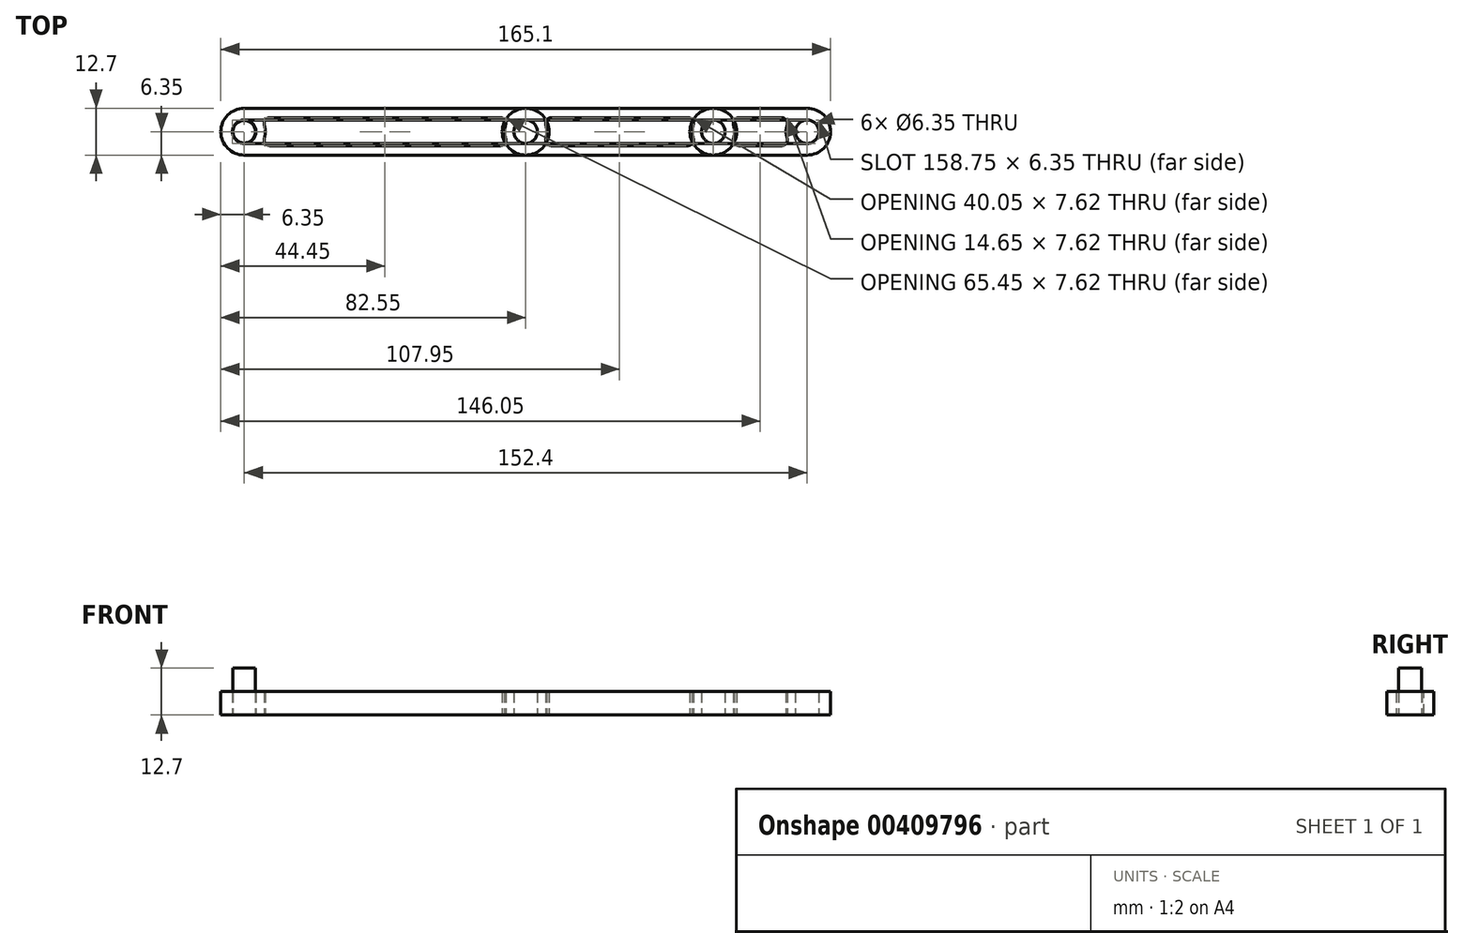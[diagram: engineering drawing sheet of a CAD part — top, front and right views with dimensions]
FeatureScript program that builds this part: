
annotation { "Feature Type Name" : "Feature", "Feature Type Description" : "" }
export const myFeature = defineFeature(function(context is Context, id is Id, definition is map)
    precondition{}
    {
        {
            var Q0;
            Q0=qCreatedBy(makeId("Top.planeOp"),FACE);
            var sketch = newSketch(context, id + "F0", { "sketchPlane" : qUnion([Q0])});
            skCircle(sketch, "E0", {"center": v(0, 0) * mm, "radius": 3.18 * mm});
            skCircle(sketch, "E1", {"center": v(0, 0) * mm, "radius": 6.35 * mm});
            skCircle(sketch, "E2", {"center": v(76.2, 0) * mm, "radius": 3.18 * mm});
            skCircle(sketch, "E3", {"center": v(127, 0) * mm, "radius": 3.18 * mm});
            skCircle(sketch, "E4", {"center": v(152.4, 0) * mm, "radius": 3.18 * mm});
            skCircle(sketch, "E5", {"center": v(76.2, 0) * mm, "radius": 6.35 * mm});
            skCircle(sketch, "E6", {"center": v(127, 0) * mm, "radius": 6.35 * mm});
            skCircle(sketch, "E7", {"center": v(152.4, 0) * mm, "radius": 6.35 * mm});
            skLineSegment(sketch, "E8", {"start": v(0, 6.35) * mm, "end": v(152.4, 6.35) * mm});
            skLineSegment(sketch, "E9", {"start": v(0, -6.35) * mm, "end": v(152.4, -6.35) * mm});
            skCircle(sketch, "E10", {"center": v(0, 0) * mm, "radius": 3.05 * mm});
            skLineSegment(sketch, "E11", {"start": v(0, 3.18) * mm, "end": v(152.4, 3.17) * mm});
            skLineSegment(sketch, "E12", {"start": v(0, -3.17) * mm, "end": v(152.4, -3.18) * mm});
            skSolve(sketch);
        }
        {
            var Q0;
            {var subQ0=sQuery(id+"F0.wireOp",EDGE,"E8");var subQ1=sQuery(id+"F0.wireOp",EDGE,"E1");var subQ2=makeQuery(id+"F0.imprint","INTERSECT",VERTEX,{"derivedFrom":[subQ1,subQ0]});Q0=makeQuery(id+"F0.imprint","IMPRINT",FACE,{"disambiguationData":[TD([[makeQuery(id+"F0.imprint","IMPRINT",EDGE,{"disambiguationData":[TD([[subQ2,1.0]])],"derivedFrom":subQ1}),-1.0]])]});}
            var Q1;
            Q1=makeQuery(id+"F0.imprint","IMPRINT",FACE,{"disambiguationData":[TD([[makeQuery(id+"F0.imprint","IMPRINT",EDGE,{"derivedFrom":sQuery(id+"F0.wireOp",EDGE,"E2")}),-1.0]])]});
            var Q2;
            Q2=makeQuery(id+"F0.imprint","IMPRINT",FACE,{"disambiguationData":[TD([[makeQuery(id+"F0.imprint","IMPRINT",EDGE,{"derivedFrom":sQuery(id+"F0.wireOp",EDGE,"E0")}),-1.0]])]});
            var Q3;
            {var subQ5=sQuery(id+"F0.wireOp",EDGE,"E11");var subQ7=sQuery(id+"F0.wireOp",EDGE,"E0");var subQ8=makeQuery(id+"F0.imprint","INTERSECT",VERTEX,{"derivedFrom":[subQ7,subQ5]});Q3=makeQuery(id+"F0.imprint","IMPRINT",FACE,{"disambiguationData":[TD([[makeQuery(id+"F0.imprint","IMPRINT",EDGE,{"disambiguationData":[TD([[subQ8,-1.0]])],"derivedFrom":subQ7}),-1.0]])]});}
            var Q4;
            {var subQ0=sQuery(id+"F0.wireOp",EDGE,"E11");var subQ1=sQuery(id+"F0.wireOp",EDGE,"E1");var subQ2=makeQuery(id+"F0.imprint","INTERSECT",VERTEX,{"derivedFrom":[subQ1,subQ0]});Q4=makeQuery(id+"F0.imprint","IMPRINT",FACE,{"disambiguationData":[TD([[makeQuery(id+"F0.imprint","IMPRINT",EDGE,{"disambiguationData":[TD([[subQ2,1.0]])],"derivedFrom":subQ1}),-1.0]])]});}
            var Q5;
            {var subQ0=sQuery(id+"F0.wireOp",EDGE,"E9");var subQ1=sQuery(id+"F0.wireOp",EDGE,"E1");var subQ2=makeQuery(id+"F0.imprint","INTERSECT",VERTEX,{"derivedFrom":[subQ1,subQ0]});Q5=makeQuery(id+"F0.imprint","IMPRINT",FACE,{"disambiguationData":[TD([[makeQuery(id+"F0.imprint","IMPRINT",EDGE,{"disambiguationData":[TD([[subQ2,-1.0]])],"derivedFrom":subQ1}),-1.0]])]});}
            var Q6;
            {var subQ0=sQuery(id+"F0.wireOp",EDGE,"E5");var subQ1=makeQuery(id+"F0.imprint","INTERSECT",VERTEX,{"derivedFrom":[subQ0,sQuery(id+"F0.wireOp",EDGE,"E8")]});Q6=makeQuery(id+"F0.imprint","IMPRINT",FACE,{"disambiguationData":[TD([[makeQuery(id+"F0.imprint","IMPRINT",EDGE,{"disambiguationData":[TD([[subQ1,1.0]])],"derivedFrom":subQ0}),1.0]])]});}
            var Q7;
            {var subQ0=sQuery(id+"F0.wireOp",EDGE,"E5");var subQ1=makeQuery(id+"F0.imprint","INTERSECT",VERTEX,{"derivedFrom":[subQ0,sQuery(id+"F0.wireOp",EDGE,"E9")]});Q7=makeQuery(id+"F0.imprint","IMPRINT",FACE,{"disambiguationData":[TD([[makeQuery(id+"F0.imprint","IMPRINT",EDGE,{"disambiguationData":[TD([[subQ1,1.0]])],"derivedFrom":subQ0}),1.0]])]});}
            extrude(context, id + "F1", {"entities" : qUnion([Q0, Q1, Q2, Q3, Q4, Q5, Q6, Q7]), "depth" : 6.35 * mm});
        }
        {
            var Q0;
            {var subQ0=sQuery(id+"F0.wireOp",EDGE,"E8");var subQ1=sQuery(id+"F0.wireOp",EDGE,"E5");var subQ2=makeQuery(id+"F0.imprint","INTERSECT",VERTEX,{"derivedFrom":[subQ1,subQ0]});Q0=makeQuery(id+"F0.imprint","IMPRINT",FACE,{"disambiguationData":[TD([[makeQuery(id+"F0.imprint","IMPRINT",EDGE,{"disambiguationData":[TD([[subQ2,1.0]])],"derivedFrom":subQ1}),-1.0]])]});}
            var Q1;
            {var subQ0=sQuery(id+"F0.wireOp",EDGE,"E11");var subQ1=sQuery(id+"F0.wireOp",EDGE,"E5");var subQ2=makeQuery(id+"F0.imprint","INTERSECT",VERTEX,{"disambiguationData":[OD(0.0)],"derivedFrom":[subQ1,subQ0]});Q1=makeQuery(id+"F0.imprint","IMPRINT",FACE,{"disambiguationData":[TD([[makeQuery(id+"F0.imprint","IMPRINT",EDGE,{"disambiguationData":[TD([[subQ2,1.0]])],"derivedFrom":subQ1}),-1.0]])]});}
            var Q2;
            {var subQ0=sQuery(id+"F0.wireOp",EDGE,"E9");var subQ1=sQuery(id+"F0.wireOp",EDGE,"E5");var subQ2=makeQuery(id+"F0.imprint","INTERSECT",VERTEX,{"derivedFrom":[subQ1,subQ0]});Q2=makeQuery(id+"F0.imprint","IMPRINT",FACE,{"disambiguationData":[TD([[makeQuery(id+"F0.imprint","IMPRINT",EDGE,{"disambiguationData":[TD([[subQ2,-1.0]])],"derivedFrom":subQ1}),-1.0]])]});}
            var Q3;
            {var subQ0=sQuery(id+"F0.wireOp",EDGE,"E11");var subQ1=sQuery(id+"F0.wireOp",EDGE,"E3");var subQ2=makeQuery(id+"F0.imprint","INTERSECT",VERTEX,{"derivedFrom":[subQ1,subQ0]});Q3=makeQuery(id+"F0.imprint","IMPRINT",FACE,{"disambiguationData":[TD([[makeQuery(id+"F0.imprint","IMPRINT",EDGE,{"disambiguationData":[TD([[subQ2,-1.0]])],"derivedFrom":subQ1}),-1.0]])]});}
            var Q4;
            {var subQ0=sQuery(id+"F0.wireOp",EDGE,"E6");var subQ1=makeQuery(id+"F0.imprint","INTERSECT",VERTEX,{"derivedFrom":[subQ0,sQuery(id+"F0.wireOp",EDGE,"E8")]});Q4=makeQuery(id+"F0.imprint","IMPRINT",FACE,{"disambiguationData":[TD([[makeQuery(id+"F0.imprint","IMPRINT",EDGE,{"disambiguationData":[TD([[subQ1,1.0]])],"derivedFrom":subQ0}),1.0]])]});}
            var Q5;
            {var subQ0=sQuery(id+"F0.wireOp",EDGE,"E11");var subQ1=sQuery(id+"F0.wireOp",EDGE,"E3");var subQ2=makeQuery(id+"F0.imprint","INTERSECT",VERTEX,{"derivedFrom":[subQ1,subQ0]});Q5=makeQuery(id+"F0.imprint","IMPRINT",FACE,{"disambiguationData":[TD([[makeQuery(id+"F0.imprint","IMPRINT",EDGE,{"disambiguationData":[TD([[subQ2,1.0]])],"derivedFrom":subQ1}),-1.0]])]});}
            var Q6;
            {var subQ0=sQuery(id+"F0.wireOp",EDGE,"E6");var subQ1=makeQuery(id+"F0.imprint","INTERSECT",VERTEX,{"derivedFrom":[subQ0,sQuery(id+"F0.wireOp",EDGE,"E9")]});Q6=makeQuery(id+"F0.imprint","IMPRINT",FACE,{"disambiguationData":[TD([[makeQuery(id+"F0.imprint","IMPRINT",EDGE,{"disambiguationData":[TD([[subQ1,1.0]])],"derivedFrom":subQ0}),1.0]])]});}
            var Q7;
            {var subQ0=sQuery(id+"F0.wireOp",EDGE,"E5");var subQ1=makeQuery(id+"F0.imprint","INTERSECT",VERTEX,{"derivedFrom":[subQ0,sQuery(id+"F0.wireOp",EDGE,"E8")]});Q7=makeQuery(id+"F0.imprint","IMPRINT",FACE,{"disambiguationData":[TD([[makeQuery(id+"F0.imprint","IMPRINT",EDGE,{"disambiguationData":[TD([[subQ1,1.0]])],"derivedFrom":subQ0}),1.0]])]});}
            var Q8;
            {var subQ0=sQuery(id+"F0.wireOp",EDGE,"E11");var subQ1=sQuery(id+"F0.wireOp",EDGE,"E2");var subQ2=makeQuery(id+"F0.imprint","INTERSECT",VERTEX,{"derivedFrom":[subQ1,subQ0]});Q8=makeQuery(id+"F0.imprint","IMPRINT",FACE,{"disambiguationData":[TD([[makeQuery(id+"F0.imprint","IMPRINT",EDGE,{"disambiguationData":[TD([[subQ2,-1.0]])],"derivedFrom":subQ1}),-1.0]])]});}
            var Q9;
            {var subQ0=sQuery(id+"F0.wireOp",EDGE,"E11");var subQ1=sQuery(id+"F0.wireOp",EDGE,"E2");var subQ2=makeQuery(id+"F0.imprint","INTERSECT",VERTEX,{"derivedFrom":[subQ1,subQ0]});Q9=makeQuery(id+"F0.imprint","IMPRINT",FACE,{"disambiguationData":[TD([[makeQuery(id+"F0.imprint","IMPRINT",EDGE,{"disambiguationData":[TD([[subQ2,1.0]])],"derivedFrom":subQ1}),-1.0]])]});}
            var Q10;
            {var subQ0=sQuery(id+"F0.wireOp",EDGE,"E5");var subQ1=makeQuery(id+"F0.imprint","INTERSECT",VERTEX,{"derivedFrom":[subQ0,sQuery(id+"F0.wireOp",EDGE,"E9")]});Q10=makeQuery(id+"F0.imprint","IMPRINT",FACE,{"disambiguationData":[TD([[makeQuery(id+"F0.imprint","IMPRINT",EDGE,{"disambiguationData":[TD([[subQ1,1.0]])],"derivedFrom":subQ0}),1.0]])]});}
            extrude(context, id + "F2", {"entities" : qUnion([Q0, Q1, Q2, Q3, Q4, Q5, Q6, Q7, Q8, Q9, Q10]), "depth" : 6.35 * mm});
        }
        {
            var Q0;
            {var subQ0=sQuery(id+"F0.wireOp",EDGE,"E8");var subQ1=sQuery(id+"F0.wireOp",EDGE,"E6");var subQ2=makeQuery(id+"F0.imprint","INTERSECT",VERTEX,{"derivedFrom":[subQ1,subQ0]});Q0=makeQuery(id+"F0.imprint","IMPRINT",FACE,{"disambiguationData":[TD([[makeQuery(id+"F0.imprint","IMPRINT",EDGE,{"disambiguationData":[TD([[subQ2,1.0]])],"derivedFrom":subQ1}),-1.0]])]});}
            var Q1;
            Q1=makeQuery(id+"F0.imprint","IMPRINT",FACE,{"disambiguationData":[TD([[makeQuery(id+"F0.imprint","IMPRINT",EDGE,{"derivedFrom":sQuery(id+"F0.wireOp",EDGE,"E3")}),-1.0]])]});
            var Q2;
            Q2=makeQuery(id+"F0.imprint","IMPRINT",FACE,{"disambiguationData":[TD([[makeQuery(id+"F0.imprint","IMPRINT",EDGE,{"derivedFrom":sQuery(id+"F0.wireOp",EDGE,"E4")}),-1.0]])]});
            var Q3;
            {var subQ0=sQuery(id+"F0.wireOp",EDGE,"E11");var subQ1=sQuery(id+"F0.wireOp",EDGE,"E6");var subQ2=makeQuery(id+"F0.imprint","INTERSECT",VERTEX,{"disambiguationData":[OD(0.0)],"derivedFrom":[subQ1,subQ0]});Q3=makeQuery(id+"F0.imprint","IMPRINT",FACE,{"disambiguationData":[TD([[makeQuery(id+"F0.imprint","IMPRINT",EDGE,{"disambiguationData":[TD([[subQ2,1.0]])],"derivedFrom":subQ1}),-1.0]])]});}
            var Q4;
            {var subQ3=sQuery(id+"F0.wireOp",EDGE,"E11");var subQ7=sQuery(id+"F0.wireOp",EDGE,"E4");var subQ8=makeQuery(id+"F0.imprint","INTERSECT",VERTEX,{"derivedFrom":[subQ7,subQ3]});Q4=makeQuery(id+"F0.imprint","IMPRINT",FACE,{"disambiguationData":[TD([[makeQuery(id+"F0.imprint","IMPRINT",EDGE,{"disambiguationData":[TD([[subQ8,1.0]])],"derivedFrom":subQ7}),-1.0]])]});}
            var Q5;
            {var subQ0=sQuery(id+"F0.wireOp",EDGE,"E9");var subQ1=sQuery(id+"F0.wireOp",EDGE,"E6");var subQ2=makeQuery(id+"F0.imprint","INTERSECT",VERTEX,{"derivedFrom":[subQ1,subQ0]});Q5=makeQuery(id+"F0.imprint","IMPRINT",FACE,{"disambiguationData":[TD([[makeQuery(id+"F0.imprint","IMPRINT",EDGE,{"disambiguationData":[TD([[subQ2,-1.0]])],"derivedFrom":subQ1}),-1.0]])]});}
            var Q6;
            {var subQ0=sQuery(id+"F0.wireOp",EDGE,"E6");var subQ1=makeQuery(id+"F0.imprint","INTERSECT",VERTEX,{"derivedFrom":[subQ0,sQuery(id+"F0.wireOp",EDGE,"E8")]});Q6=makeQuery(id+"F0.imprint","IMPRINT",FACE,{"disambiguationData":[TD([[makeQuery(id+"F0.imprint","IMPRINT",EDGE,{"disambiguationData":[TD([[subQ1,1.0]])],"derivedFrom":subQ0}),1.0]])]});}
            var Q7;
            {var subQ0=sQuery(id+"F0.wireOp",EDGE,"E6");var subQ1=makeQuery(id+"F0.imprint","INTERSECT",VERTEX,{"derivedFrom":[subQ0,sQuery(id+"F0.wireOp",EDGE,"E9")]});Q7=makeQuery(id+"F0.imprint","IMPRINT",FACE,{"disambiguationData":[TD([[makeQuery(id+"F0.imprint","IMPRINT",EDGE,{"disambiguationData":[TD([[subQ1,1.0]])],"derivedFrom":subQ0}),1.0]])]});}
            extrude(context, id + "F3", {"entities" : qUnion([Q0, Q1, Q2, Q3, Q4, Q5, Q6, Q7]), "depth" : 6.35 * mm});
        }
        {
            var Q0;
            {var subQ5=sQuery(id+"F0.wireOp",EDGE,"E11");var subQ7=sQuery(id+"F0.wireOp",EDGE,"E0");var subQ8=makeQuery(id+"F0.imprint","INTERSECT",VERTEX,{"derivedFrom":[subQ7,subQ5]});Q0=makeQuery(id+"F0.imprint","IMPRINT",FACE,{"disambiguationData":[TD([[makeQuery(id+"F0.imprint","IMPRINT",EDGE,{"disambiguationData":[TD([[subQ8,-1.0]])],"derivedFrom":subQ7}),-1.0]])]});}
            var Q1;
            {var subQ0=sQuery(id+"F0.wireOp",EDGE,"E8");var subQ1=sQuery(id+"F0.wireOp",EDGE,"E1");var subQ2=makeQuery(id+"F0.imprint","INTERSECT",VERTEX,{"derivedFrom":[subQ1,subQ0]});Q1=makeQuery(id+"F0.imprint","IMPRINT",FACE,{"disambiguationData":[TD([[makeQuery(id+"F0.imprint","IMPRINT",EDGE,{"disambiguationData":[TD([[subQ2,1.0]])],"derivedFrom":subQ1}),-1.0]])]});}
            var Q2;
            {var subQ0=sQuery(id+"F0.wireOp",EDGE,"E5");var subQ1=makeQuery(id+"F0.imprint","INTERSECT",VERTEX,{"derivedFrom":[subQ0,sQuery(id+"F0.wireOp",EDGE,"E8")]});Q2=makeQuery(id+"F0.imprint","IMPRINT",FACE,{"disambiguationData":[TD([[makeQuery(id+"F0.imprint","IMPRINT",EDGE,{"disambiguationData":[TD([[subQ1,1.0]])],"derivedFrom":subQ0}),1.0]])]});}
            var Q3;
            {var subQ0=sQuery(id+"F0.wireOp",EDGE,"E9");var subQ1=sQuery(id+"F0.wireOp",EDGE,"E1");var subQ2=makeQuery(id+"F0.imprint","INTERSECT",VERTEX,{"derivedFrom":[subQ1,subQ0]});Q3=makeQuery(id+"F0.imprint","IMPRINT",FACE,{"disambiguationData":[TD([[makeQuery(id+"F0.imprint","IMPRINT",EDGE,{"disambiguationData":[TD([[subQ2,-1.0]])],"derivedFrom":subQ1}),-1.0]])]});}
            var Q4;
            {var subQ0=sQuery(id+"F0.wireOp",EDGE,"E5");var subQ1=makeQuery(id+"F0.imprint","INTERSECT",VERTEX,{"derivedFrom":[subQ0,sQuery(id+"F0.wireOp",EDGE,"E9")]});Q4=makeQuery(id+"F0.imprint","IMPRINT",FACE,{"disambiguationData":[TD([[makeQuery(id+"F0.imprint","IMPRINT",EDGE,{"disambiguationData":[TD([[subQ1,1.0]])],"derivedFrom":subQ0}),1.0]])]});}
            var Q5;
            {var subQ0=sQuery(id+"F0.wireOp",EDGE,"E8");var subQ1=sQuery(id+"F0.wireOp",EDGE,"E5");var subQ2=makeQuery(id+"F0.imprint","INTERSECT",VERTEX,{"derivedFrom":[subQ1,subQ0]});Q5=makeQuery(id+"F0.imprint","IMPRINT",FACE,{"disambiguationData":[TD([[makeQuery(id+"F0.imprint","IMPRINT",EDGE,{"disambiguationData":[TD([[subQ2,1.0]])],"derivedFrom":subQ1}),-1.0]])]});}
            var Q6;
            {var subQ0=sQuery(id+"F0.wireOp",EDGE,"E6");var subQ1=makeQuery(id+"F0.imprint","INTERSECT",VERTEX,{"derivedFrom":[subQ0,sQuery(id+"F0.wireOp",EDGE,"E8")]});Q6=makeQuery(id+"F0.imprint","IMPRINT",FACE,{"disambiguationData":[TD([[makeQuery(id+"F0.imprint","IMPRINT",EDGE,{"disambiguationData":[TD([[subQ1,1.0]])],"derivedFrom":subQ0}),1.0]])]});}
            var Q7;
            {var subQ0=sQuery(id+"F0.wireOp",EDGE,"E8");var subQ1=sQuery(id+"F0.wireOp",EDGE,"E6");var subQ2=makeQuery(id+"F0.imprint","INTERSECT",VERTEX,{"derivedFrom":[subQ1,subQ0]});Q7=makeQuery(id+"F0.imprint","IMPRINT",FACE,{"disambiguationData":[TD([[makeQuery(id+"F0.imprint","IMPRINT",EDGE,{"disambiguationData":[TD([[subQ2,1.0]])],"derivedFrom":subQ1}),-1.0]])]});}
            var Q8;
            {var subQ3=sQuery(id+"F0.wireOp",EDGE,"E11");var subQ7=sQuery(id+"F0.wireOp",EDGE,"E4");var subQ8=makeQuery(id+"F0.imprint","INTERSECT",VERTEX,{"derivedFrom":[subQ7,subQ3]});Q8=makeQuery(id+"F0.imprint","IMPRINT",FACE,{"disambiguationData":[TD([[makeQuery(id+"F0.imprint","IMPRINT",EDGE,{"disambiguationData":[TD([[subQ8,1.0]])],"derivedFrom":subQ7}),-1.0]])]});}
            var Q9;
            {var subQ0=sQuery(id+"F0.wireOp",EDGE,"E9");var subQ1=sQuery(id+"F0.wireOp",EDGE,"E6");var subQ2=makeQuery(id+"F0.imprint","INTERSECT",VERTEX,{"derivedFrom":[subQ1,subQ0]});Q9=makeQuery(id+"F0.imprint","IMPRINT",FACE,{"disambiguationData":[TD([[makeQuery(id+"F0.imprint","IMPRINT",EDGE,{"disambiguationData":[TD([[subQ2,-1.0]])],"derivedFrom":subQ1}),-1.0]])]});}
            var Q10;
            {var subQ0=sQuery(id+"F0.wireOp",EDGE,"E6");var subQ1=makeQuery(id+"F0.imprint","INTERSECT",VERTEX,{"derivedFrom":[subQ0,sQuery(id+"F0.wireOp",EDGE,"E9")]});Q10=makeQuery(id+"F0.imprint","IMPRINT",FACE,{"disambiguationData":[TD([[makeQuery(id+"F0.imprint","IMPRINT",EDGE,{"disambiguationData":[TD([[subQ1,1.0]])],"derivedFrom":subQ0}),1.0]])]});}
            var Q11;
            {var subQ0=sQuery(id+"F0.wireOp",EDGE,"E9");var subQ1=sQuery(id+"F0.wireOp",EDGE,"E5");var subQ2=makeQuery(id+"F0.imprint","INTERSECT",VERTEX,{"derivedFrom":[subQ1,subQ0]});Q11=makeQuery(id+"F0.imprint","IMPRINT",FACE,{"disambiguationData":[TD([[makeQuery(id+"F0.imprint","IMPRINT",EDGE,{"disambiguationData":[TD([[subQ2,-1.0]])],"derivedFrom":subQ1}),-1.0]])]});}
            extrude(context, id + "F4", {"entities" : qUnion([Q0, Q1, Q2, Q3, Q4, Q5, Q6, Q7, Q8, Q9, Q10, Q11]), "depth" : 6.35 * mm});
        }
        {
            var Q0;
            Q0=makeQuery(id+"F0.imprint","IMPRINT",FACE,{"disambiguationData":[TD([[makeQuery(id+"F0.imprint","IMPRINT",EDGE,{"derivedFrom":sQuery(id+"F0.wireOp",EDGE,"E10")}),1.0]])]});
            extrude(context, id + "F5", {"entities" : qUnion([Q0]), "depth" : 12.7 * mm});
        }
        {
            var Q0;
            Q0=makeQuery(id+"F1.opExtrude","CAP_FACE",FACE,{"disambiguationData":[OSD([sQuery(id+"F0.wireOp",EDGE,"E0"),sQuery(id+"F0.wireOp",EDGE,"E1"),sQuery(id+"F0.wireOp",EDGE,"E2"),sQuery(id+"F0.wireOp",EDGE,"E5"),sQuery(id+"F0.wireOp",EDGE,"E8"),sQuery(id+"F0.wireOp",EDGE,"E9")])],"isStart":false});
            var Q1;
            Q1=makeQuery(id+"F1.opExtrude","CAP_FACE",FACE,{"disambiguationData":[OSD([sQuery(id+"F0.wireOp",EDGE,"E0"),sQuery(id+"F0.wireOp",EDGE,"E1"),sQuery(id+"F0.wireOp",EDGE,"E2"),sQuery(id+"F0.wireOp",EDGE,"E5"),sQuery(id+"F0.wireOp",EDGE,"E8"),sQuery(id+"F0.wireOp",EDGE,"E9")])],"isStart":true});
            shell(context, id + "F6", {"entities" : qUnion([Q0, Q1]), "thickness" : 2.54 * mm});
        }
        {
            var Q0;
            Q0=makeQuery(id+"F2.opExtrude","CAP_FACE",FACE,{"disambiguationData":[OSD([sQuery(id+"F0.wireOp",EDGE,"E2"),sQuery(id+"F0.wireOp",EDGE,"E3"),sQuery(id+"F0.wireOp",EDGE,"E5"),sQuery(id+"F0.wireOp",EDGE,"E6"),sQuery(id+"F0.wireOp",EDGE,"E8"),sQuery(id+"F0.wireOp",EDGE,"E9")])],"isStart":false});
            var Q1;
            Q1=makeQuery(id+"F2.opExtrude","CAP_FACE",FACE,{"disambiguationData":[OSD([sQuery(id+"F0.wireOp",EDGE,"E2"),sQuery(id+"F0.wireOp",EDGE,"E3"),sQuery(id+"F0.wireOp",EDGE,"E5"),sQuery(id+"F0.wireOp",EDGE,"E6"),sQuery(id+"F0.wireOp",EDGE,"E8"),sQuery(id+"F0.wireOp",EDGE,"E9")])],"isStart":true});
            shell(context, id + "F7", {"entities" : qUnion([Q0, Q1]), "thickness" : 2.54 * mm});
        }
        {
            var Q0;
            Q0=makeQuery(id+"F3.opExtrude","CAP_FACE",FACE,{"disambiguationData":[OSD([sQuery(id+"F0.wireOp",EDGE,"E3"),sQuery(id+"F0.wireOp",EDGE,"E4"),sQuery(id+"F0.wireOp",EDGE,"E6"),sQuery(id+"F0.wireOp",EDGE,"E7"),sQuery(id+"F0.wireOp",EDGE,"E8"),sQuery(id+"F0.wireOp",EDGE,"E9")])],"isStart":false});
            var Q1;
            Q1=makeQuery(id+"F3.opExtrude","CAP_FACE",FACE,{"disambiguationData":[OSD([sQuery(id+"F0.wireOp",EDGE,"E3"),sQuery(id+"F0.wireOp",EDGE,"E4"),sQuery(id+"F0.wireOp",EDGE,"E6"),sQuery(id+"F0.wireOp",EDGE,"E7"),sQuery(id+"F0.wireOp",EDGE,"E8"),sQuery(id+"F0.wireOp",EDGE,"E9")])],"isStart":true});
            shell(context, id + "F8", {"entities" : qUnion([Q0, Q1]), "thickness" : 2.54 * mm});
        }
        {
            var Q0;
            Q0=makeQuery(id+"F6.opShell","TWEAK_EDGE",EDGE,{"derivedFrom":[makeQuery(id+"F1.opExtrude","SWEPT_FACE",FACE,{"disambiguationData":[OSD([sQuery(id+"F0.wireOp",EDGE,"E2")])]}),makeQuery(id+"F1.opExtrude","SWEPT_FACE",FACE,{"disambiguationData":[OSD([sQuery(id+"F0.wireOp",EDGE,"E8")])]})]});
            var Q1;
            Q1=makeQuery(id+"F6.opShell","TWEAK_EDGE",EDGE,{"derivedFrom":[makeQuery(id+"F1.opExtrude","SWEPT_FACE",FACE,{"disambiguationData":[OSD([sQuery(id+"F0.wireOp",EDGE,"E2")])]}),makeQuery(id+"F1.opExtrude","SWEPT_FACE",FACE,{"disambiguationData":[OSD([sQuery(id+"F0.wireOp",EDGE,"E9")])]})]});
            var Q2;
            Q2=makeQuery(id+"F6.opShell","TWEAK_EDGE",EDGE,{"derivedFrom":[makeQuery(id+"F1.opExtrude","SWEPT_FACE",FACE,{"disambiguationData":[OSD([sQuery(id+"F0.wireOp",EDGE,"E0")])]}),makeQuery(id+"F1.opExtrude","SWEPT_FACE",FACE,{"disambiguationData":[OSD([sQuery(id+"F0.wireOp",EDGE,"E8")])]})]});
            var Q3;
            Q3=makeQuery(id+"F6.opShell","TWEAK_EDGE",EDGE,{"derivedFrom":[makeQuery(id+"F1.opExtrude","SWEPT_FACE",FACE,{"disambiguationData":[OSD([sQuery(id+"F0.wireOp",EDGE,"E0")])]}),makeQuery(id+"F1.opExtrude","SWEPT_FACE",FACE,{"disambiguationData":[OSD([sQuery(id+"F0.wireOp",EDGE,"E9")])]})]});
            fillet(context, id + "F9", {"entities" : qUnion([Q0, Q1, Q2, Q3]), "radius" : 1.59 * mm, "tangentPropagation" : true, "allowEdgeOverflow" : false});
        }
        {
            var Q0;
            Q0=makeQuery(id+"F7.opShell","TWEAK_EDGE",EDGE,{"derivedFrom":[makeQuery(id+"F2.opExtrude","SWEPT_FACE",FACE,{"disambiguationData":[OSD([sQuery(id+"F0.wireOp",EDGE,"E2")])]}),makeQuery(id+"F2.opExtrude","SWEPT_FACE",FACE,{"disambiguationData":[OSD([sQuery(id+"F0.wireOp",EDGE,"E8")])]})]});
            var Q1;
            Q1=makeQuery(id+"F7.opShell","TWEAK_EDGE",EDGE,{"derivedFrom":[makeQuery(id+"F2.opExtrude","SWEPT_FACE",FACE,{"disambiguationData":[OSD([sQuery(id+"F0.wireOp",EDGE,"E2")])]}),makeQuery(id+"F2.opExtrude","SWEPT_FACE",FACE,{"disambiguationData":[OSD([sQuery(id+"F0.wireOp",EDGE,"E9")])]})]});
            var Q2;
            Q2=makeQuery(id+"F7.opShell","TWEAK_EDGE",EDGE,{"derivedFrom":[makeQuery(id+"F2.opExtrude","SWEPT_FACE",FACE,{"disambiguationData":[OSD([sQuery(id+"F0.wireOp",EDGE,"E3")])]}),makeQuery(id+"F2.opExtrude","SWEPT_FACE",FACE,{"disambiguationData":[OSD([sQuery(id+"F0.wireOp",EDGE,"E8")])]})]});
            var Q3;
            Q3=makeQuery(id+"F7.opShell","TWEAK_EDGE",EDGE,{"derivedFrom":[makeQuery(id+"F2.opExtrude","SWEPT_FACE",FACE,{"disambiguationData":[OSD([sQuery(id+"F0.wireOp",EDGE,"E3")])]}),makeQuery(id+"F2.opExtrude","SWEPT_FACE",FACE,{"disambiguationData":[OSD([sQuery(id+"F0.wireOp",EDGE,"E9")])]})]});
            fillet(context, id + "F10", {"entities" : qUnion([Q0, Q1, Q2, Q3]), "radius" : 1.59 * mm, "tangentPropagation" : true, "allowEdgeOverflow" : false});
        }
        {
            var Q0;
            Q0=makeQuery(id+"F8.opShell","TWEAK_EDGE",EDGE,{"derivedFrom":[makeQuery(id+"F3.opExtrude","SWEPT_FACE",FACE,{"disambiguationData":[OSD([sQuery(id+"F0.wireOp",EDGE,"E3")])]}),makeQuery(id+"F3.opExtrude","SWEPT_FACE",FACE,{"disambiguationData":[OSD([sQuery(id+"F0.wireOp",EDGE,"E8")])]})]});
            var Q1;
            Q1=makeQuery(id+"F8.opShell","TWEAK_EDGE",EDGE,{"derivedFrom":[makeQuery(id+"F3.opExtrude","SWEPT_FACE",FACE,{"disambiguationData":[OSD([sQuery(id+"F0.wireOp",EDGE,"E3")])]}),makeQuery(id+"F3.opExtrude","SWEPT_FACE",FACE,{"disambiguationData":[OSD([sQuery(id+"F0.wireOp",EDGE,"E9")])]})]});
            var Q2;
            Q2=makeQuery(id+"F8.opShell","TWEAK_EDGE",EDGE,{"derivedFrom":[makeQuery(id+"F3.opExtrude","SWEPT_FACE",FACE,{"disambiguationData":[OSD([sQuery(id+"F0.wireOp",EDGE,"E4")])]}),makeQuery(id+"F3.opExtrude","SWEPT_FACE",FACE,{"disambiguationData":[OSD([sQuery(id+"F0.wireOp",EDGE,"E8")])]})]});
            var Q3;
            Q3=makeQuery(id+"F8.opShell","TWEAK_EDGE",EDGE,{"derivedFrom":[makeQuery(id+"F3.opExtrude","SWEPT_FACE",FACE,{"disambiguationData":[OSD([sQuery(id+"F0.wireOp",EDGE,"E4")])]}),makeQuery(id+"F3.opExtrude","SWEPT_FACE",FACE,{"disambiguationData":[OSD([sQuery(id+"F0.wireOp",EDGE,"E9")])]})]});
            fillet(context, id + "F11", {"entities" : qUnion([Q0, Q1, Q2, Q3]), "radius" : 1.59 * mm, "tangentPropagation" : true, "allowEdgeOverflow" : false});
        }
    });
